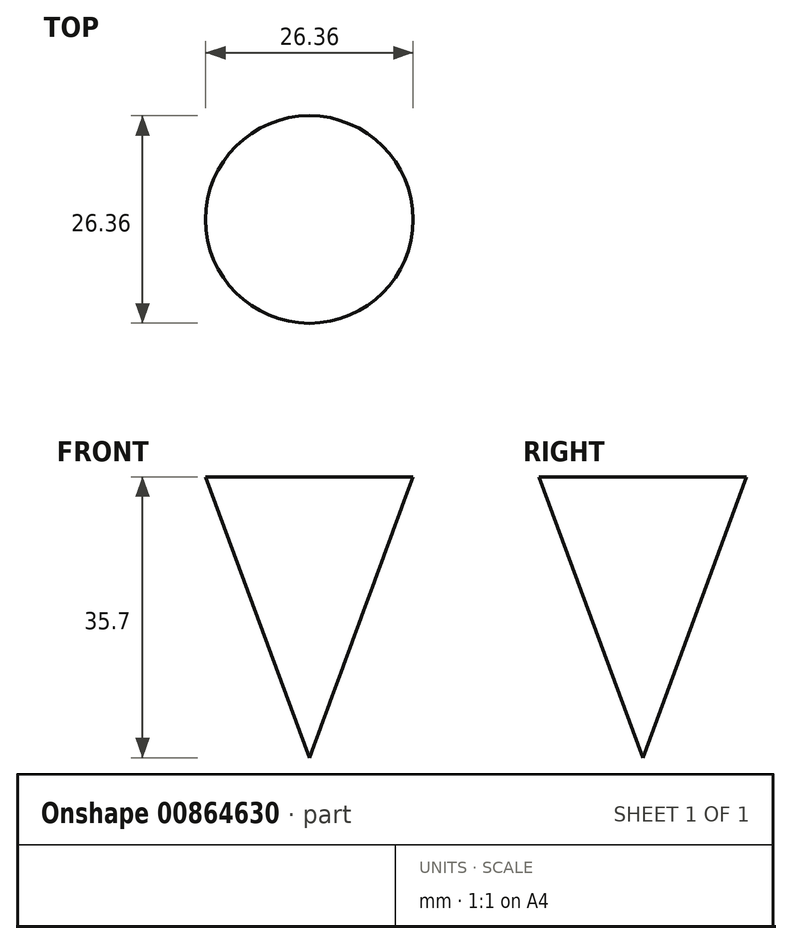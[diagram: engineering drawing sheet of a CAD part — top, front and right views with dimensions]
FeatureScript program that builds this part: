
annotation { "Feature Type Name" : "Feature", "Feature Type Description" : "" }
export const myFeature = defineFeature(function(context is Context, id is Id, definition is map)
    precondition{}
    {
        {
            var Q0;
            Q0=qCreatedBy(makeId("Front.planeOp"),FACE);
            var sketch = newSketch(context, id + "F0", { "sketchPlane" : qUnion([Q0])});
            skLineSegment(sketch, "E0", {"start": v(0, 0) * mm, "end": v(-13.18, 0) * mm});
            skLineSegment(sketch, "E1", {"start": v(0, 0) * mm, "end": v(0, -35.7) * mm});
            skLineSegment(sketch, "E2", {"start": v(-13.18, 0) * mm, "end": v(0, -35.7) * mm});
            skSolve(sketch);
        }
        {
            var Q0;
            Q0 = qSketchRegion(id + "F0", true);
            var Q1;
            Q1=sQuery(id+"F0.wireOp",EDGE,"E1");
            revolve(context, id + "F1", {"surfaceOperationType" : NewSurfaceOperationType.NEW, "entities" : qUnion([Q0]), "axis" : qUnion([Q1]), "revolveType" : RevolveType.FULL});
        }
    });
